# Revit family: Circular_Ottoman_BIM
name_source: partatom
category: Arredi
units: mm (PartAtom-declared; Revit-internal decimal feet)

## family parameters
Attiva taglio nelle viste = No
Basato su piano di lavoro = No
Condiviso = No
Numero OmniClass = 23.40.20.00
Origine composizione di rendering = Geometria famiglia
Punto di calcolo locali = No
Sempre verticale = Sì
Taglio con vuoti quando caricato = No
Titolo OmniClass = General Furniture and Specialties

## types (1)
- CB-264
    AVAILABLE FINISHES = Black powder coat finish (BP), or satin nickel (SN), satin brass (SB), bronze (BZ) or gunmetal (GM) nanoceramic coated solid stainless steel.
    BASE MATERIAL = BASSAM_FELLOWS_MATT_BLACK_BP
    BIM BADGE = https://bim.archiproducts.com
    COLLECTION = CIRCULAR
    DIAMETER = 600 mm
    Descrizione = Upholstered ottoman with steel base
    HEIGHT = 350 mm  [stored 1.14829 ft]
    MATERIAL DESCRIPTION = Stainless steel base. Foam upholstery with double topstitch, CARB2 plywood inner frame.
    Modello = Circular Ottoman
    PRODUCT CODE = CB-264
    PRODUCT SHEET = https://www.archiproducts.com
    Produttore = BassamFellows
    Prospetto di default = 0 mm  [stored 0 ft]
    TECHNICAL SHEET = https://bassamfellows.com
    UPHOLSTERY MATERIAL = BASSAM_FELLOWS_ELEGANT_LEATHER_48027_OLIVE
    URL = https://bassamfellows.com

note: [stored X ft] marks values corroborated as IEEE doubles in the binary element streams (Revit-internal decimal feet)

## geometry (parser evidence)
native form markers: Sweep x2
no freeform markers — native parametric forms only
